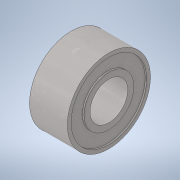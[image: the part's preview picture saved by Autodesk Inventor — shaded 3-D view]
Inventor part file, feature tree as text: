
AUTODESK INVENTOR PART (.ipt)
format: ipt  version: 2020 (Build 240168000, 168)  size: 175,104 bytes
history: native  units: mm
features: other x1, revolve x1, sketch x1
ambient origin geometry x8: Origin, YZ Plane, XZ Plane, XY Plane, X Axis, Y Axis, Z Axis, Center Point
bodies: Volumenkörper1 (feature_tree)
feature tree (3):
  other  "Kugellager 685-ZZ-C3"
  revolve  "Umdrehung1"
  sketch  "Skizze1"  dims[d0=5.0mm d1=11.0mm d2=5.0mm d3=0.2mm d4=0.8mm d5=0.5mm d6=90.0deg]
